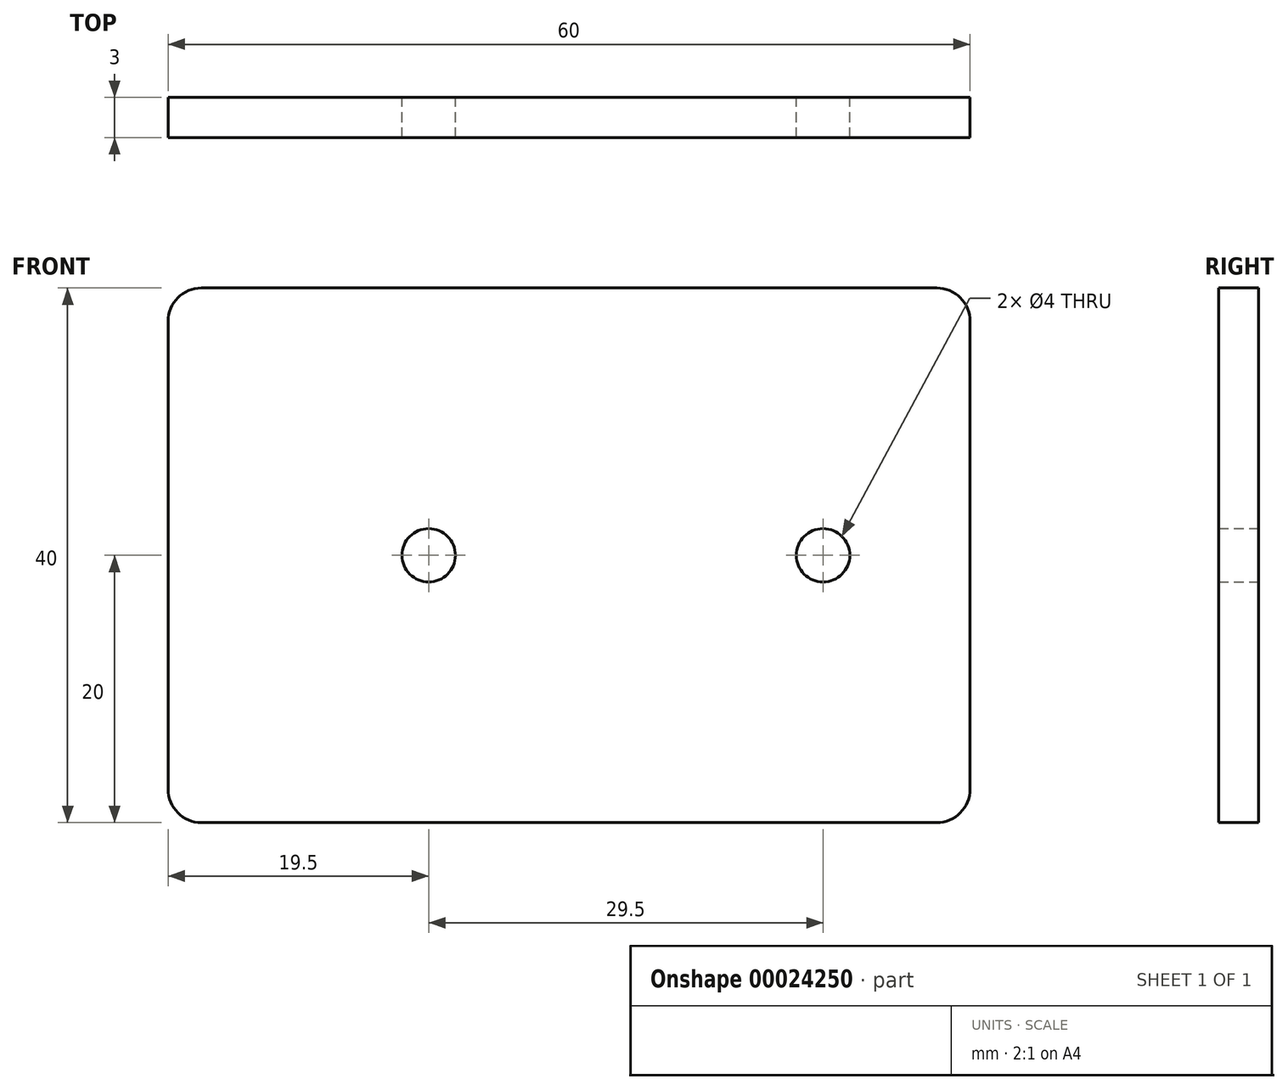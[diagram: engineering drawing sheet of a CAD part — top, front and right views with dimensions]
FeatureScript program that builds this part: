
annotation { "Feature Type Name" : "Feature", "Feature Type Description" : "" }
export const myFeature = defineFeature(function(context is Context, id is Id, definition is map)
    precondition{}
    {
        {
            var Q0;
            Q0=qCreatedBy(makeId("Front.planeOp"),FACE);
            var sketch = newSketch(context, id + "F0", { "sketchPlane" : qUnion([Q0])});
            skLineSegment(sketch, "E0.rect.bottom", {"start": v(-27.5, 20) * mm, "end": v(27.5, 20) * mm});
            skLineSegment(sketch, "E0.rect.top", {"start": v(-27.5, -20) * mm, "end": v(27.5, -20) * mm});
            skLineSegment(sketch, "E0.rect.left", {"start": v(-30, 17.5) * mm, "end": v(-30, -17.5) * mm});
            skLineSegment(sketch, "E0.rect.right", {"start": v(30, 17.5) * mm, "end": v(30, -17.5) * mm});
            skPoint(sketch, "E0.rect.middle", {"position": v(0, 0) * mm});
            skPoint(sketch, "E1.visualSharp", {"position": v(-30, 20) * mm});
            skArc(sketch, "E1.filletArc", {"start": v(-27.5, 20) * mm, "mid": v(-29.27, 19.27) * mm, "end": v(-30, 17.5) * mm});
            skPoint(sketch, "E2.visualSharp", {"position": v(30, 20) * mm});
            skArc(sketch, "E2.filletArc", {"start": v(30, 17.5) * mm, "mid": v(29.27, 19.27) * mm, "end": v(27.5, 20) * mm});
            skPoint(sketch, "E3.visualSharp", {"position": v(30, -20) * mm});
            skArc(sketch, "E3.filletArc", {"start": v(27.5, -20) * mm, "mid": v(29.27, -19.27) * mm, "end": v(30, -17.5) * mm});
            skPoint(sketch, "E4.visualSharp", {"position": v(-30, -20) * mm});
            skArc(sketch, "E4.filletArc", {"start": v(-30, -17.5) * mm, "mid": v(-29.27, -19.27) * mm, "end": v(-27.5, -20) * mm});
            skLineSegment(sketch, "E5", {"start": v(-30, 0) * mm, "end": v(-10.5, 0) * mm});
            skLineSegment(sketch, "E6", {"start": v(-10.5, 0) * mm, "end": v(6.34, 0) * mm});
            skLineSegment(sketch, "E7", {"start": v(30, 0) * mm, "end": v(19, 0) * mm});
            skCircle(sketch, "E8", {"center": v(-10.5, 0) * mm, "radius": 2 * mm});
            skCircle(sketch, "E9", {"center": v(19, 0) * mm, "radius": 2 * mm});
            skSolve(sketch);
        }
        {
            var Q0;
            Q0=makeQuery(id+"F0.imprint","IMPRINT",FACE,{"disambiguationData":[TD([[makeQuery(id+"F0.imprint","IMPRINT",EDGE,{"derivedFrom":sQuery(id+"F0.wireOp",EDGE,"E0.rect.bottom")}),-1.0]])]});
            extrude(context, id + "F1", {"entities" : qUnion([Q0]), "depth" : 3 * mm});
        }
    });
